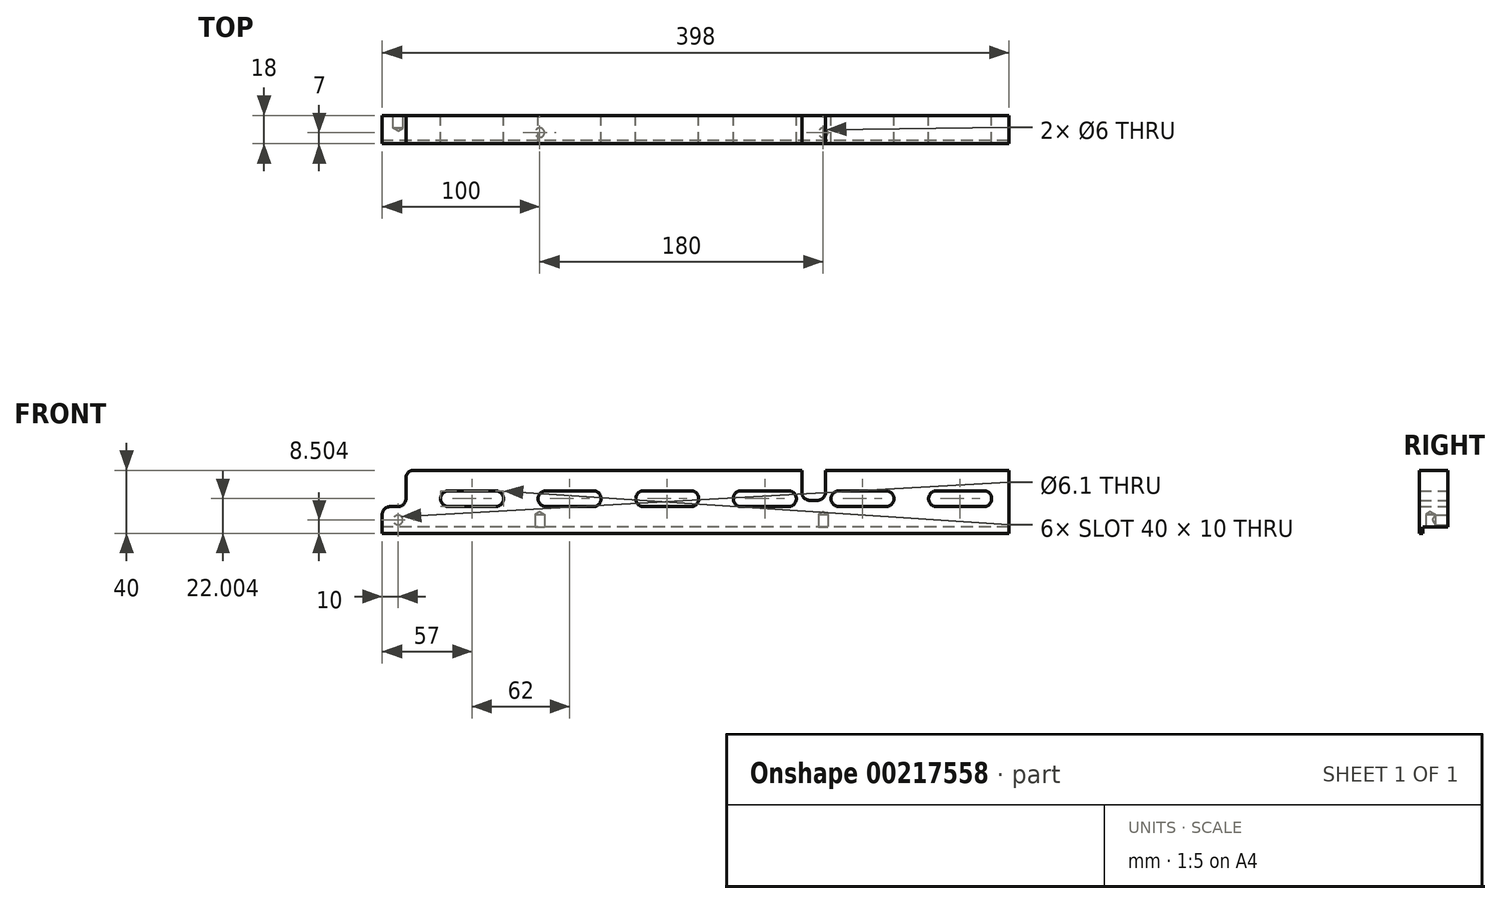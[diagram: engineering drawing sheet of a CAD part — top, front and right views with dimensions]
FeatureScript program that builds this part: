
annotation { "Feature Type Name" : "Feature", "Feature Type Description" : "" }
export const myFeature = defineFeature(function(context is Context, id is Id, definition is map)
    precondition{}
    {
        {
            var Q0;
            Q0=qCreatedBy(makeId("Front.planeOp"),FACE);
            var sketch = newSketch(context, id + "F0", { "sketchPlane" : qUnion([Q0])});
            skLineSegment(sketch, "E0", {"start": v(-402.9, -12.17) * mm, "end": v(-402.9, -24.17) * mm});
            skLineSegment(sketch, "E1", {"start": v(-4.9, -24.17) * mm, "end": v(-4.9, 15.83) * mm});
            skLineSegment(sketch, "E2", {"start": v(-4.9, -24.17) * mm, "end": v(-402.9, -24.17) * mm});
            skLineSegment(sketch, "E3", {"start": v(-397.9, -7.17) * mm, "end": v(-392.9, -7.17) * mm});
            skLineSegment(sketch, "E4", {"start": v(-387.9, -2.17) * mm, "end": v(-387.9, 10.83) * mm});
            skLineSegment(sketch, "E5", {"start": v(-382.9, 15.83) * mm, "end": v(-136.4, 15.83) * mm});
            skLineSegment(sketch, "E6", {"start": v(-136.4, 15.83) * mm, "end": v(-136.4, 1.83) * mm});
            skLineSegment(sketch, "E7", {"start": v(-121.4, 1.83) * mm, "end": v(-121.4, 15.83) * mm});
            skLineSegment(sketch, "E8", {"start": v(-121.4, 15.83) * mm, "end": v(-4.9, 15.83) * mm});
            skLineSegment(sketch, "E9", {"start": v(-20.9, -7.17) * mm, "end": v(-50.9, -7.17) * mm});
            skLineSegment(sketch, "E10", {"start": v(-50.9, 2.83) * mm, "end": v(-20.9, 2.83) * mm});
            skLineSegment(sketch, "E11", {"start": v(-82.9, -7.17) * mm, "end": v(-112.9, -7.17) * mm});
            skLineSegment(sketch, "E12", {"start": v(-112.9, 2.83) * mm, "end": v(-82.9, 2.83) * mm});
            skLineSegment(sketch, "E13", {"start": v(-126.4, -3.17) * mm, "end": v(-131.4, -3.17) * mm});
            skLineSegment(sketch, "E14", {"start": v(-144.9, -7.17) * mm, "end": v(-174.9, -7.17) * mm});
            skLineSegment(sketch, "E15", {"start": v(-174.9, 2.83) * mm, "end": v(-144.9, 2.83) * mm});
            skLineSegment(sketch, "E16", {"start": v(-206.9, -7.17) * mm, "end": v(-236.9, -7.17) * mm});
            skLineSegment(sketch, "E17", {"start": v(-236.9, 2.83) * mm, "end": v(-206.9, 2.83) * mm});
            skLineSegment(sketch, "E18", {"start": v(-268.9, -7.17) * mm, "end": v(-298.9, -7.17) * mm});
            skLineSegment(sketch, "E19", {"start": v(-298.9, 2.83) * mm, "end": v(-268.9, 2.83) * mm});
            skLineSegment(sketch, "E20", {"start": v(-330.9, -7.17) * mm, "end": v(-360.9, -7.17) * mm});
            skLineSegment(sketch, "E21", {"start": v(-360.9, 2.83) * mm, "end": v(-330.9, 2.83) * mm});
            skArc(sketch, "E22", {"start": v(-330.9, -7.17) * mm, "mid": v(-325.9, -2.17) * mm, "end": v(-330.9, 2.83) * mm});
            skArc(sketch, "E23", {"start": v(-360.9, 2.83) * mm, "mid": v(-365.9, -2.17) * mm, "end": v(-360.9, -7.17) * mm});
            skArc(sketch, "E24", {"start": v(-397.9, -7.17) * mm, "mid": v(-401.44, -8.63) * mm, "end": v(-402.9, -12.17) * mm});
            skArc(sketch, "E25", {"start": v(-392.9, -7.17) * mm, "mid": v(-389.36, -5.7) * mm, "end": v(-387.9, -2.17) * mm});
            skArc(sketch, "E26", {"start": v(-387.9, 10.83) * mm, "mid": v(-386.44, 14.37) * mm, "end": v(-382.9, 15.83) * mm});
            skArc(sketch, "E27", {"start": v(-298.9, 2.83) * mm, "mid": v(-303.9, -2.17) * mm, "end": v(-298.9, -7.17) * mm});
            skArc(sketch, "E28", {"start": v(-268.9, 2.83) * mm, "mid": v(-263.9, -2.17) * mm, "end": v(-268.9, -7.17) * mm});
            skArc(sketch, "E29", {"start": v(-236.9, 2.83) * mm, "mid": v(-241.9, -2.17) * mm, "end": v(-236.9, -7.17) * mm});
            skArc(sketch, "E30", {"start": v(-206.9, 2.83) * mm, "mid": v(-201.9, -2.17) * mm, "end": v(-206.9, -7.17) * mm});
            skArc(sketch, "E31", {"start": v(-174.9, 2.83) * mm, "mid": v(-179.9, -2.17) * mm, "end": v(-174.9, -7.17) * mm});
            skArc(sketch, "E32", {"start": v(-144.9, 2.83) * mm, "mid": v(-139.9, -2.17) * mm, "end": v(-144.9, -7.17) * mm});
            skArc(sketch, "E33", {"start": v(-112.9, 2.83) * mm, "mid": v(-117.9, -2.17) * mm, "end": v(-112.9, -7.17) * mm});
            skArc(sketch, "E34", {"start": v(-121.4, 1.83) * mm, "mid": v(-122.86, -1.7) * mm, "end": v(-126.4, -3.17) * mm});
            skArc(sketch, "E35", {"start": v(-136.4, 1.83) * mm, "mid": v(-134.94, -1.7) * mm, "end": v(-131.4, -3.17) * mm});
            skArc(sketch, "E36", {"start": v(-82.9, 2.83) * mm, "mid": v(-77.9, -2.17) * mm, "end": v(-82.9, -7.17) * mm});
            skArc(sketch, "E37", {"start": v(-50.9, 2.83) * mm, "mid": v(-55.9, -2.17) * mm, "end": v(-50.9, -7.17) * mm});
            skArc(sketch, "E38", {"start": v(-20.9, 2.83) * mm, "mid": v(-15.9, -2.17) * mm, "end": v(-20.9, -7.17) * mm});
            skSolve(sketch);
        }
        {
            var Q0;
            Q0 = qSketchRegion(id + "F0", true);
            extrude(context, id + "F1", {"entities" : qUnion([Q0]), "depth" : 18 * mm});
        }
        {
            var Q0;
            Q0=makeQuery(id+"F1.opExtrude","SWEPT_FACE",FACE,{"disambiguationData":[OSD([sQuery(id+"F0.wireOp",EDGE,"E0")])]});
            var sketch = newSketch(context, id + "F2", { "sketchPlane" : qUnion([Q0])});
            skLineSegment(sketch, "E39", {"start": v(0, -24.17) * mm, "end": v(0, -20.17) * mm});
            skLineSegment(sketch, "E40", {"start": v(0, -24.17) * mm, "end": v(16, -24.17) * mm});
            skLineSegment(sketch, "E41", {"start": v(0, -20.17) * mm, "end": v(16, -20.17) * mm});
            skLineSegment(sketch, "E42", {"start": v(16, -20.17) * mm, "end": v(16, -24.17) * mm});
            skSolve(sketch);
        }
        {
            var Q0;
            Q0 = qSketchRegion(id + "F2", true);
            extrude(context, id + "F3", {"entities" : qUnion([Q0]), "operationType" : NewBodyOperationType.REMOVE, "oppositeDirection" : true, "depth" : 400 * mm});
        }
        {
            var Q0;
            Q0=makeQuery(id+"F3.boolean.opBoolean","COPY",FACE,{"derivedFrom":makeQuery(id+"F3.opExtrude","SWEPT_FACE",FACE,{"disambiguationData":[OSD([sQuery(id+"F2.wireOp",EDGE,"E41")])]})});
            var sketch = newSketch(context, id + "F4", { "sketchPlane" : qUnion([Q0])});
            skCircle(sketch, "E43", {"center": v(-122.9, 11) * mm, "radius": 3 * mm});
            skCircle(sketch, "E44", {"center": v(-302.9, 11) * mm, "radius": 3 * mm});
            skSolve(sketch);
        }
        {
            var Q0;
            Q0=sQuery(id+"F4.wireOp",VERTEX,"E44.center");
            var Q1;
            Q1=sQuery(id+"F4.wireOp",VERTEX,"E43.center");
            var Q2;
            Q2=makeQuery(id+"F1.opExtrude","SWEPT_BODY",BODY,{"disambiguationData":[OSD([sQuery(id+"F0.wireOp",EDGE,"E0"),sQuery(id+"F0.wireOp",EDGE,"E1"),sQuery(id+"F0.wireOp",EDGE,"E2"),sQuery(id+"F0.wireOp",EDGE,"E3"),sQuery(id+"F0.wireOp",EDGE,"E4"),sQuery(id+"F0.wireOp",EDGE,"E5"),sQuery(id+"F0.wireOp",EDGE,"E6"),sQuery(id+"F0.wireOp",EDGE,"E7"),sQuery(id+"F0.wireOp",EDGE,"E8"),sQuery(id+"F0.wireOp",EDGE,"E9"),sQuery(id+"F0.wireOp",EDGE,"E10"),sQuery(id+"F0.wireOp",EDGE,"E11"),sQuery(id+"F0.wireOp",EDGE,"E12"),sQuery(id+"F0.wireOp",EDGE,"E13"),sQuery(id+"F0.wireOp",EDGE,"E14"),sQuery(id+"F0.wireOp",EDGE,"E15"),sQuery(id+"F0.wireOp",EDGE,"E16"),sQuery(id+"F0.wireOp",EDGE,"E17"),sQuery(id+"F0.wireOp",EDGE,"E18"),sQuery(id+"F0.wireOp",EDGE,"E19"),sQuery(id+"F0.wireOp",EDGE,"E20"),sQuery(id+"F0.wireOp",EDGE,"E21"),sQuery(id+"F0.wireOp",EDGE,"E22"),sQuery(id+"F0.wireOp",EDGE,"E23"),sQuery(id+"F0.wireOp",EDGE,"E24"),sQuery(id+"F0.wireOp",EDGE,"E25"),sQuery(id+"F0.wireOp",EDGE,"E26"),sQuery(id+"F0.wireOp",EDGE,"E27"),sQuery(id+"F0.wireOp",EDGE,"E28"),sQuery(id+"F0.wireOp",EDGE,"E29"),sQuery(id+"F0.wireOp",EDGE,"E30"),sQuery(id+"F0.wireOp",EDGE,"E31"),sQuery(id+"F0.wireOp",EDGE,"E32"),sQuery(id+"F0.wireOp",EDGE,"E33"),sQuery(id+"F0.wireOp",EDGE,"E34"),sQuery(id+"F0.wireOp",EDGE,"E35"),sQuery(id+"F0.wireOp",EDGE,"E36"),sQuery(id+"F0.wireOp",EDGE,"E37"),sQuery(id+"F0.wireOp",EDGE,"E38")])]});
            hole(context, id + "F5", {"style" : HoleStyle.SIMPLE, "endStyle" : HoleEndStyle.BLIND, "standardTappedOrClearance" : lookupTablePath({ "standard" : "ISO", "size" : "6", "type" : "Drilled" }), "standardBlindInLast" : lookupTablePath({ "standard" : "ISO", "size" : "6", "type" : "Drilled" }), "holeDiameter" : 6 * mm, "holeDepth" : 8 * mm, "startFromSketch" : true, "locations" : qUnion([Q0, Q1]), "scope" : qUnion([Q2])});
        }
        {
            var Q0;
            Q0=makeQuery(id+"F1.opExtrude","CAP_FACE",FACE,{"disambiguationData":[OSD([sQuery(id+"F0.wireOp",EDGE,"E0"),sQuery(id+"F0.wireOp",EDGE,"E1"),sQuery(id+"F0.wireOp",EDGE,"E2"),sQuery(id+"F0.wireOp",EDGE,"E3"),sQuery(id+"F0.wireOp",EDGE,"E4"),sQuery(id+"F0.wireOp",EDGE,"E5"),sQuery(id+"F0.wireOp",EDGE,"E6"),sQuery(id+"F0.wireOp",EDGE,"E7"),sQuery(id+"F0.wireOp",EDGE,"E8"),sQuery(id+"F0.wireOp",EDGE,"E9"),sQuery(id+"F0.wireOp",EDGE,"E10"),sQuery(id+"F0.wireOp",EDGE,"E11"),sQuery(id+"F0.wireOp",EDGE,"E12"),sQuery(id+"F0.wireOp",EDGE,"E13"),sQuery(id+"F0.wireOp",EDGE,"E14"),sQuery(id+"F0.wireOp",EDGE,"E15"),sQuery(id+"F0.wireOp",EDGE,"E16"),sQuery(id+"F0.wireOp",EDGE,"E17"),sQuery(id+"F0.wireOp",EDGE,"E18"),sQuery(id+"F0.wireOp",EDGE,"E19"),sQuery(id+"F0.wireOp",EDGE,"E20"),sQuery(id+"F0.wireOp",EDGE,"E21"),sQuery(id+"F0.wireOp",EDGE,"E22"),sQuery(id+"F0.wireOp",EDGE,"E23"),sQuery(id+"F0.wireOp",EDGE,"E24"),sQuery(id+"F0.wireOp",EDGE,"E25"),sQuery(id+"F0.wireOp",EDGE,"E26"),sQuery(id+"F0.wireOp",EDGE,"E27"),sQuery(id+"F0.wireOp",EDGE,"E28"),sQuery(id+"F0.wireOp",EDGE,"E29"),sQuery(id+"F0.wireOp",EDGE,"E30"),sQuery(id+"F0.wireOp",EDGE,"E31"),sQuery(id+"F0.wireOp",EDGE,"E32"),sQuery(id+"F0.wireOp",EDGE,"E33"),sQuery(id+"F0.wireOp",EDGE,"E34"),sQuery(id+"F0.wireOp",EDGE,"E35"),sQuery(id+"F0.wireOp",EDGE,"E36"),sQuery(id+"F0.wireOp",EDGE,"E37"),sQuery(id+"F0.wireOp",EDGE,"E38")])],"isStart":true});
            var sketch = newSketch(context, id + "F6", { "sketchPlane" : qUnion([Q0])});
            skLineSegment(sketch, "E45", {"start": v(402.9, -20.17) * mm, "end": v(392.9, -20.17) * mm});
            skLineSegment(sketch, "E46", {"start": v(392.9, -20.17) * mm, "end": v(392.9, -15.67) * mm});
            skCircle(sketch, "E47", {"center": v(392.9, -15.67) * mm, "radius": 3.05 * mm});
            skSolve(sketch);
        }
        {
            var Q0;
            Q0=sQuery(id+"F6.wireOp",VERTEX,"E47.center");
            var Q1;
            Q1=makeQuery(id+"F1.opExtrude","SWEPT_BODY",BODY,{"disambiguationData":[OSD([sQuery(id+"F0.wireOp",EDGE,"E0"),sQuery(id+"F0.wireOp",EDGE,"E1"),sQuery(id+"F0.wireOp",EDGE,"E2"),sQuery(id+"F0.wireOp",EDGE,"E3"),sQuery(id+"F0.wireOp",EDGE,"E4"),sQuery(id+"F0.wireOp",EDGE,"E5"),sQuery(id+"F0.wireOp",EDGE,"E6"),sQuery(id+"F0.wireOp",EDGE,"E7"),sQuery(id+"F0.wireOp",EDGE,"E8"),sQuery(id+"F0.wireOp",EDGE,"E9"),sQuery(id+"F0.wireOp",EDGE,"E10"),sQuery(id+"F0.wireOp",EDGE,"E11"),sQuery(id+"F0.wireOp",EDGE,"E12"),sQuery(id+"F0.wireOp",EDGE,"E13"),sQuery(id+"F0.wireOp",EDGE,"E14"),sQuery(id+"F0.wireOp",EDGE,"E15"),sQuery(id+"F0.wireOp",EDGE,"E16"),sQuery(id+"F0.wireOp",EDGE,"E17"),sQuery(id+"F0.wireOp",EDGE,"E18"),sQuery(id+"F0.wireOp",EDGE,"E19"),sQuery(id+"F0.wireOp",EDGE,"E20"),sQuery(id+"F0.wireOp",EDGE,"E21"),sQuery(id+"F0.wireOp",EDGE,"E22"),sQuery(id+"F0.wireOp",EDGE,"E23"),sQuery(id+"F0.wireOp",EDGE,"E24"),sQuery(id+"F0.wireOp",EDGE,"E25"),sQuery(id+"F0.wireOp",EDGE,"E26"),sQuery(id+"F0.wireOp",EDGE,"E27"),sQuery(id+"F0.wireOp",EDGE,"E28"),sQuery(id+"F0.wireOp",EDGE,"E29"),sQuery(id+"F0.wireOp",EDGE,"E30"),sQuery(id+"F0.wireOp",EDGE,"E31"),sQuery(id+"F0.wireOp",EDGE,"E32"),sQuery(id+"F0.wireOp",EDGE,"E33"),sQuery(id+"F0.wireOp",EDGE,"E34"),sQuery(id+"F0.wireOp",EDGE,"E35"),sQuery(id+"F0.wireOp",EDGE,"E36"),sQuery(id+"F0.wireOp",EDGE,"E37"),sQuery(id+"F0.wireOp",EDGE,"E38")])]});
            hole(context, id + "F7", {"style" : HoleStyle.SIMPLE, "endStyle" : HoleEndStyle.BLIND, "holeDiameter" : 6.1 * mm, "holeDepth" : 8 * mm, "startFromSketch" : true, "locations" : qUnion([Q0]), "scope" : qUnion([Q1])});
        }
    });
